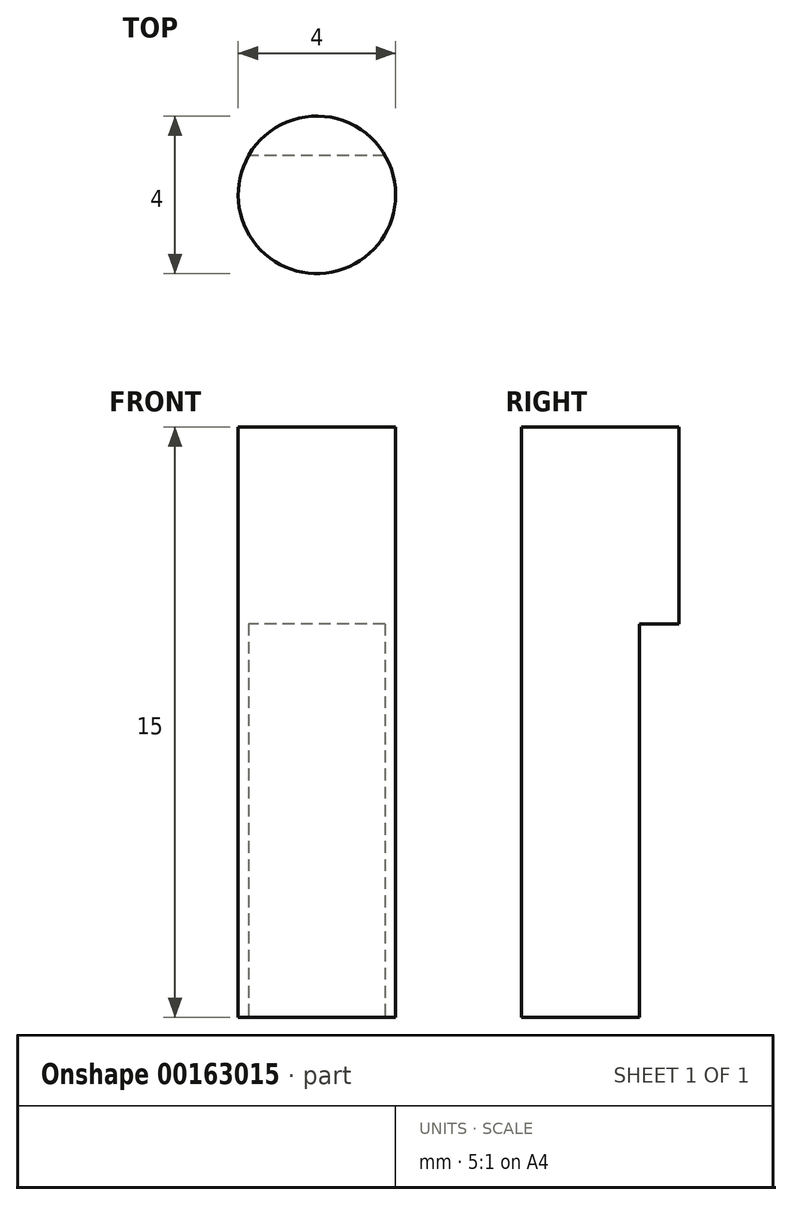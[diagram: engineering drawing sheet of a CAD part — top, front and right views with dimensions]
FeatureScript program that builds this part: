
annotation { "Feature Type Name" : "Feature", "Feature Type Description" : "" }
export const myFeature = defineFeature(function(context is Context, id is Id, definition is map)
    precondition{}
    {
        {
            var Q0;
            Q0=qCreatedBy(makeId("Top.planeOp"),FACE);
            var sketch = newSketch(context, id + "F0", { "sketchPlane" : qUnion([Q0])});
            skCircle(sketch, "E0", {"center": v(0, 0) * mm, "radius": 2 * mm});
            skSolve(sketch);
        }
        {
            var Q0;
            Q0=makeQuery(id+"F0.imprint","IMPRINT",FACE,{"disambiguationData":[TD([[makeQuery(id+"F0.imprint","IMPRINT",EDGE,{"derivedFrom":sQuery(id+"F0.wireOp",EDGE,"E0")}),1.0]])]});
            extrude(context, id + "F1", {"entities" : qUnion([Q0]), "depth" : 15 * mm});
        }
        {
            var Q0;
            Q0=makeQuery(id+"F1.opExtrude","CAP_FACE",FACE,{"disambiguationData":[OSD([sQuery(id+"F0.wireOp",EDGE,"E0")])],"isStart":true});
            var sketch = newSketch(context, id + "F3", { "sketchPlane" : qUnion([Q0])});
            skLineSegment(sketch, "E1.bottom", {"start": v(1.73, -2) * mm, "end": v(-1.73, -2) * mm});
            skLineSegment(sketch, "E1.top", {"start": v(1.73, -1) * mm, "end": v(-1.73, -1) * mm});
            skLineSegment(sketch, "E1.left", {"start": v(1.73, -2) * mm, "end": v(1.73, -1) * mm});
            skLineSegment(sketch, "E1.right", {"start": v(-1.73, -2) * mm, "end": v(-1.73, -1) * mm});
            skPoint(sketch, "E1.middle", {"position": v(0, -1.5) * mm});
            skSolve(sketch);
        }
        {
            var Q0;
            {var subQ0=sQuery(id+"F3.wireOp",EDGE,"E1.top");Q0=makeQuery(id+"F3.imprint","IMPRINT",FACE,{"disambiguationData":[TD([[makeQuery(id+"F3.imprint","IMPRINT",EDGE,{"derivedFrom":subQ0}),1.0]])]});}
            extrude(context, id + "F2", {"entities" : qUnion([Q0]), "operationType" : NewBodyOperationType.REMOVE, "oppositeDirection" : true, "depth" : 10 * mm});
        }
    });
